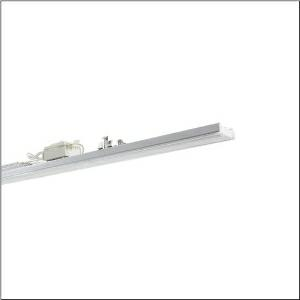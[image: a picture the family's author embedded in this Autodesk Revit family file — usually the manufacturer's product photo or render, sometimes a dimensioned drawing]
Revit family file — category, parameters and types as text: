
# Revit family: licross_r__21_recessed_mo_52tl12dn47xg_42f8
name_source: partatom
category: Lighting Fixtures
units: mm (PartAtom-declared; Revit-internal decimal feet)

## family parameters
Cut with Voids When Loaded = No
Host = Face
Light Source = No
Part Type = Normal
Room Calculation Point = No
Round Connector Dimension = Use Diameter
Shared = No

## types (1)
- --- (1 x LED, 7230 lm, 39.3 W, 4000K)
    Apparent Load = 39 VA
    CIE Flux Codes = 72 92 99 100 100
    Color Rendering = 80
    Color Temperature = 4000K
    Default Elevation = 1800 mm
    Description = Licross® 21 Recessed MO, luminaire insert, of sheet steel, galvanised, coil coated, white, length: 1.500mm, width: 66mm, height: 67mm, LED rated luminous flux: 7.230lm, light colour: 840, control gear: DALI 2, with plug, 5-pole, with phase selection, mains connection: 220..240V, AC, 50/60Hz, rated input power: 39W, halogen-free wiring, primary optical cover: cover, of PMMA, light emission: direct distribution, primary light characteristic: symmetric, protection rating (complete): IP40, insulation class (complete): insulation class I (protective earthing), certification: CE, ENEC, VDE, UKCA, protection symbol: D if used in an environment without relevant dust loads with corresponding accessories, impact resistance: IK06, permissible ambient temperature for indoor applications: -25..+40°C, corresponds to IFS (International Featured Standards) requirements for safety and quality in the food industry, reducing of maximum allowable ambient temperature of 5°C with ceiling mounting, LABS conformity tested according to VDMA 24364:2018-05, packaging unit: 1 piece
    Height = 58 mm
    Lamp = 1 x LED
    Lamp Light Flux = 7230 lm
    Lamp Power = 39.3 W
    Lamp count = 1
    Length = 1500 mm
    Luminous efficacy = 184 lm/W
    Manufacturer = Siteco
    ModVariant = No
    Model = 52TL12DN47XG
    Mounting Place = Ceiling
    Mounting Type = Pendant
    Number of Poles = 1
    OnlyDefault = Yes
    Power Factor = 1
    Product Name = Licross® 21 Recessed MO
    Product group = luminaire insert
    ProductGroupID = 902
    Protection Class = Protection class I
    Protection Degree = IP 40
    RLX_Detail_Level = 1
    RLX_Emergency_Light_Flux = 0 lm
    RLX_Emergency_Type = 0
    RLX_Emergency_Type_DB = No
    RlxData = <blob elided: 24185 chars, md5=c01b5a6c>
    Socket = socket
    Standby Power = 0 W
    System Light Flux = 7230 lm
    System Power = 39 W
    Type Comments = factory setting: luminous flux: 100 % | dim-lin: 254 | 267 mA
    Type Image = l_1296930.jpg
    URL = http://relux.com
    VarID = @adj_126290
    Voltage = 0 V
    Weight = 0.00 kg
    Width = 66 mm

## geometry (parser evidence)
native form markers: Blend x4, Sweep x10
no freeform markers — native parametric forms only
